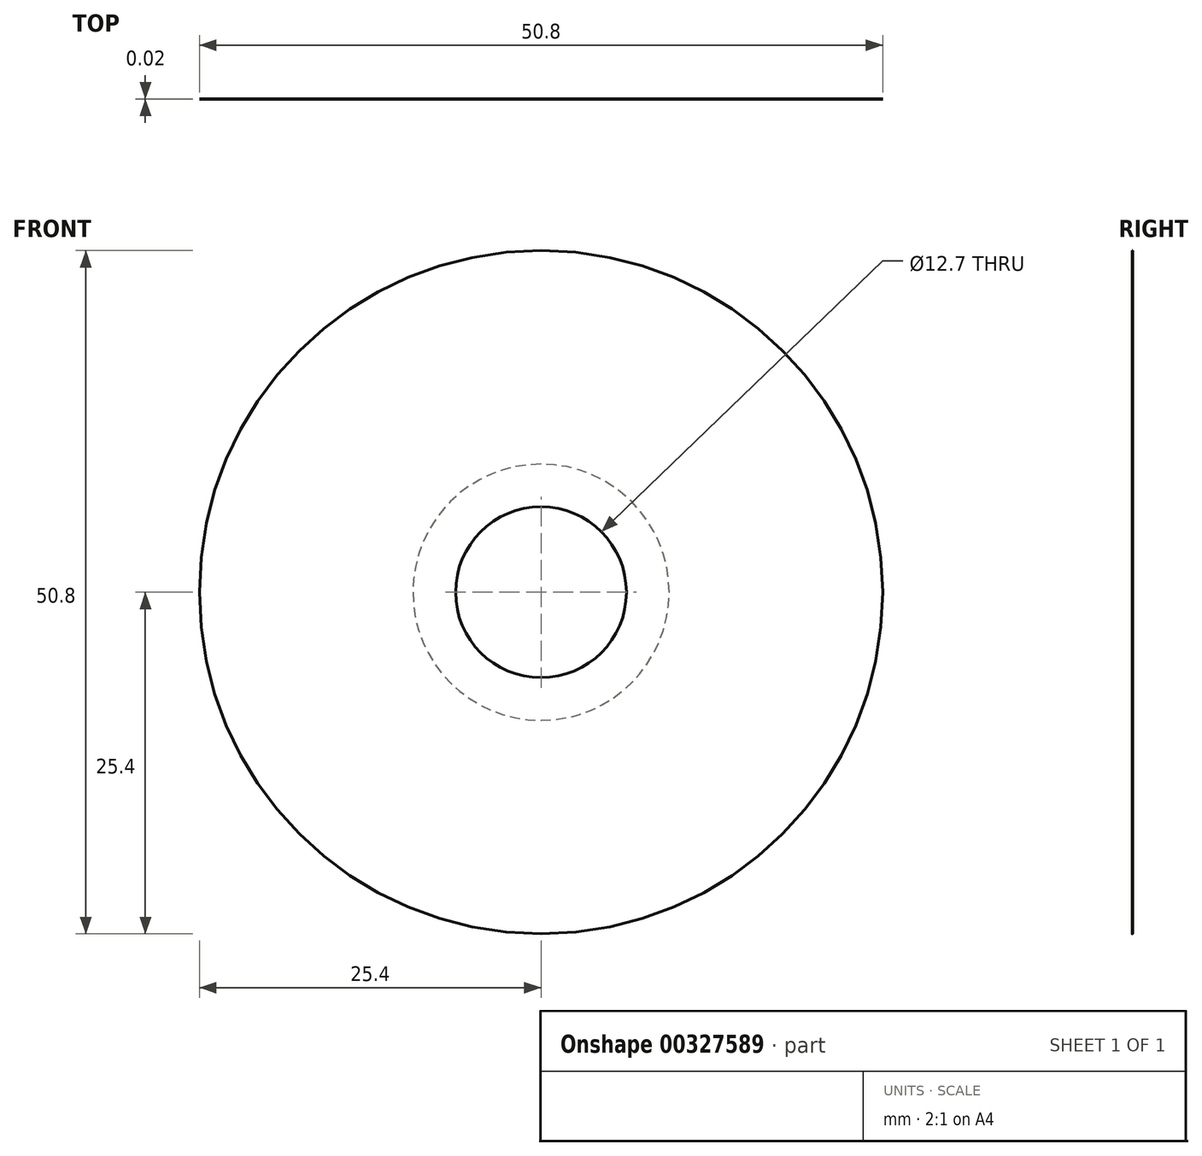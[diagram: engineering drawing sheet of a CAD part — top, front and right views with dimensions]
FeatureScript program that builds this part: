
annotation { "Feature Type Name" : "Feature", "Feature Type Description" : "" }
export const myFeature = defineFeature(function(context is Context, id is Id, definition is map)
    precondition{}
    {
        {
            var Q0;
            Q0=qCreatedBy(makeId("Front.planeOp"),FACE);
            var sketch = newSketch(context, id + "F0", { "sketchPlane" : qUnion([Q0])});
            skCircle(sketch, "E0", {"center": v(0, 0) * mm, "radius": 9.53 * mm});
            skLineSegment(sketch, "E1", {"start": v(0, 0) * mm, "end": v(9.53, 0) * mm});
            skSolve(sketch);
        }
        {
            var Q0;
            Q0 = qSketchRegion(id + "F0", true);
            extrude(context, id + "F1", {"entities" : qUnion([Q0]), "depth" : 3 / 203.2 * mm});
        }
        {
            var Q0;
            Q0=makeQuery(id+"F1.opExtrude","CAP_FACE",FACE,{"disambiguationData":[OSD([sQuery(id+"F0.wireOp",EDGE,"E0")])],"isStart":false});
            var sketch = newSketch(context, id + "F2", { "sketchPlane" : qUnion([Q0])});
            skCircle(sketch, "E2", {"center": v(0, 0) * mm, "radius": 25.4 * mm});
            skLineSegment(sketch, "E3", {"start": v(0, 0) * mm, "end": v(25.4, 0) * mm});
            skSolve(sketch);
        }
        {
            var Q0;
            Q0 = qSketchRegion(id + "F2", true);
            extrude(context, id + "F3", {"entities" : qUnion([Q0]), "operationType" : NewBodyOperationType.ADD, "oppositeDirection" : true, "depth" : 1 / 203.2 * mm});
        }
        {
            var Q0;
            Q0=makeQuery(id+"F3.boolean.opBoolean","MERGE",FACE,{"derivedFrom":[makeQuery(id+"F1.opExtrude","CAP_FACE",FACE,{"disambiguationData":[OSD([sQuery(id+"F0.wireOp",EDGE,"E0")])],"isStart":false}),makeQuery(id+"F3.opExtrude","CAP_FACE",FACE,{"disambiguationData":[OSD([sQuery(id+"F2.wireOp",EDGE,"E2")])],"isStart":true})]});
            var sketch = newSketch(context, id + "F4", { "sketchPlane" : qUnion([Q0])});
            skCircle(sketch, "E4", {"center": v(0, 0) * mm, "radius": 6.35 * mm});
            skLineSegment(sketch, "E5", {"start": v(0, 0) * mm, "end": v(6.35, 0) * mm});
            skSolve(sketch);
        }
        {
            var Q0;
            Q0 = qSketchRegion(id + "F4", true);
            extrude(context, id + "F5", {"entities" : qUnion([Q0]), "operationType" : NewBodyOperationType.REMOVE, "endBound" : BoundingType.SYMMETRIC, "oppositeDirection" : true, "depth" : 25.4 * mm});
        }
        {
            var Q0;
            Q0=makeQuery(id+"F1.opExtrude","SWEPT_BODY",BODY,{"disambiguationData":[OSD([sQuery(id+"F0.wireOp",EDGE,"E0")])]});
            var Q1;
            Q1=qCreatedBy(makeId("Front.planeOp"),FACE);
            mirror(context, id + "F6", {"operationType" : NewBodyOperationType.ADD, "entities" : qUnion([Q0]), "mirrorPlane" : qUnion([Q1])});
        }
    });
